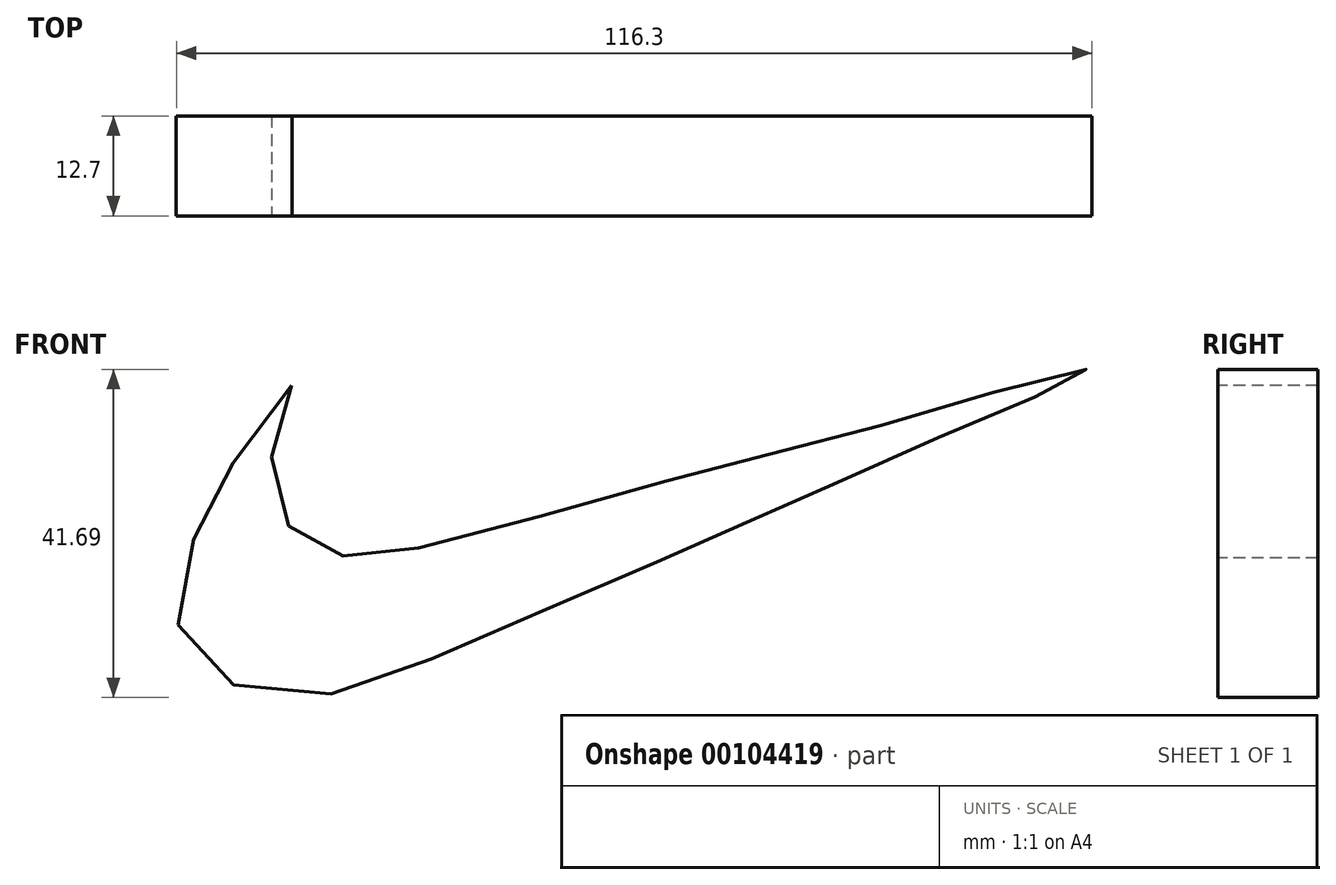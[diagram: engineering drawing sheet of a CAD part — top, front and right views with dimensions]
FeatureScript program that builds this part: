
annotation { "Feature Type Name" : "Feature", "Feature Type Description" : "" }
export const myFeature = defineFeature(function(context is Context, id is Id, definition is map)
    precondition{}
    {
        {
            var Q0;
            Q0=qCreatedBy(makeId("Front.planeOp"),FACE);
            var sketch = newSketch(context, id + "F0", { "sketchPlane" : qUnion([Q0])});
            skFitSpline(sketch, "E0", {"points": [v(-66.3, 17.27) * mm, v(-72.52, 9.45) * mm, v(-76.96, 1.46) * mm, v(-80.34, -6.36) * mm, v(-80.34, -14.53) * mm, v(-75.18, -20.04) * mm, v(-65.23, -22.35) * mm, v(-53.68, -19.5) * mm, v(-40.54, -14) * mm, v(-24.01, -6.9) * mm, v(-12.29, -1.74) * mm, v(-4.11, 1.81) * mm, v(7.8, 7.14) * mm, v(19.7, 12.3) * mm, v(30.71, 16.92) * mm, v(35.33, 19.23) * mm, v(30, 18.51) * mm, v(18.28, 14.96) * mm, v(2.64, 10.7) * mm, v(-10.33, 7.32) * mm, v(-23.3, 3.95) * mm, v(-43.38, -1.74) * mm, v(-54.75, -4.23) * mm, v(-59.73, -4.4) * mm, v(-63.28, -2.63) * mm, v(-67.19, 0) * mm, v(-68.79, 5.9) * mm, v(-68.25, 11.59) * mm, v(-66.3, 17.27) * mm]});
            skSolve(sketch);
        }
        {
            var Q0;
            Q0=makeQuery(id+"F0.imprint","IMPRINT",FACE,{"disambiguationData":[TD([[makeQuery(id+"F0.imprint","IMPRINT",EDGE,{"derivedFrom":sQuery(id+"F0.wireOp",EDGE,"E0")}),1.0]])]});
            extrude(context, id + "F1", {"entities" : qUnion([Q0]), "depth" : 6.35 * mm});
        }
        {
            var Q0;
            Q0 = qSketchRegion(id + "F0", true);
            extrude(context, id + "F2", {"entities" : qUnion([Q0]), "operationType" : NewBodyOperationType.ADD, "depth" : 12.7 * mm});
        }
    });
